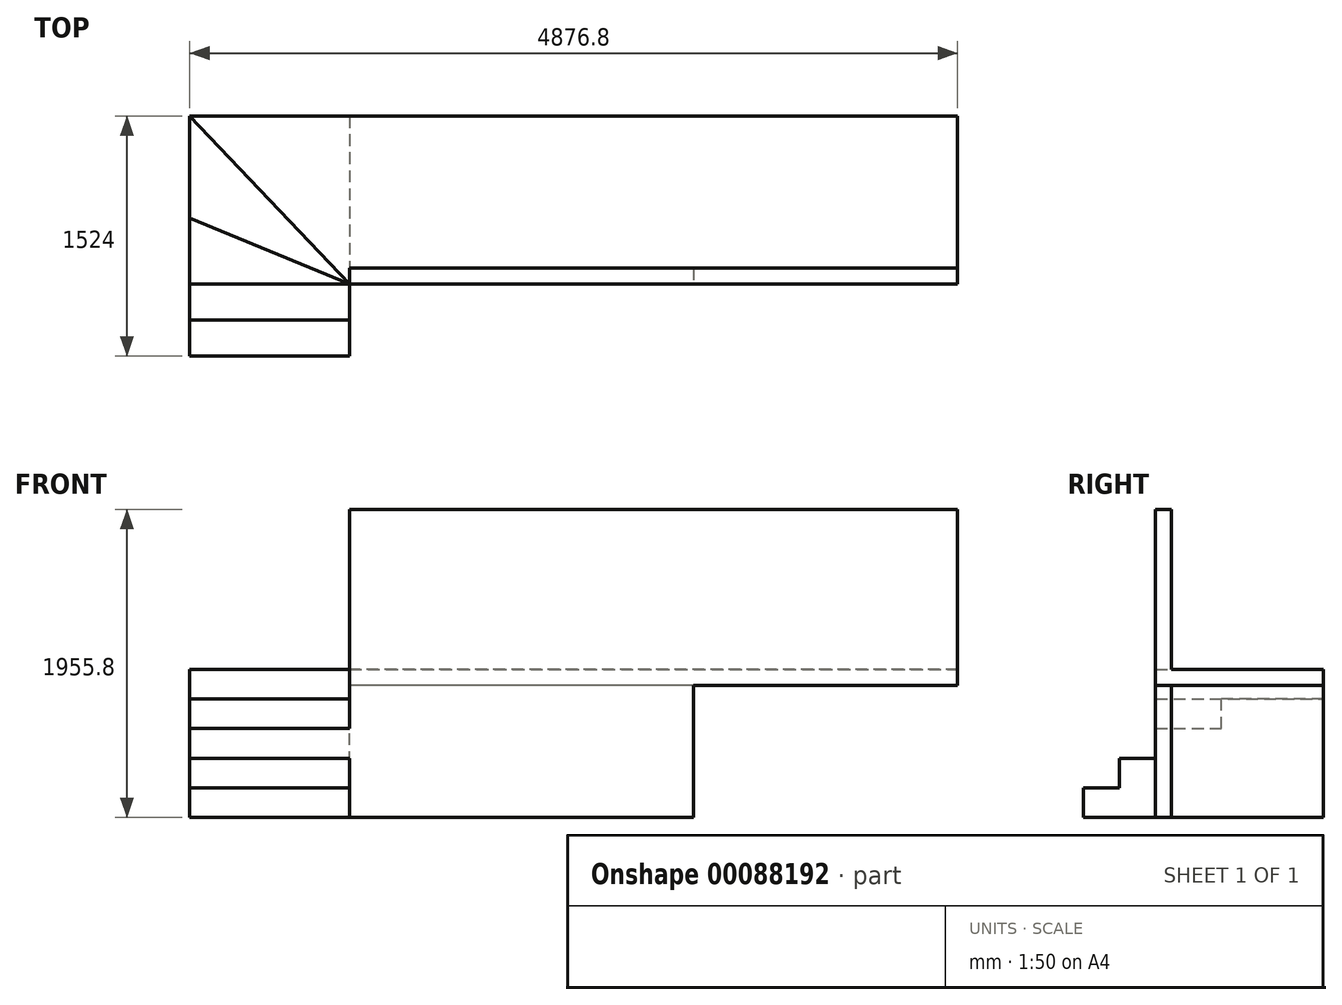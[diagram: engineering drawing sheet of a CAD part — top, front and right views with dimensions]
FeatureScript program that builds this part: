
annotation { "Feature Type Name" : "Feature", "Feature Type Description" : "" }
export const myFeature = defineFeature(function(context is Context, id is Id, definition is map)
    precondition{}
    {
        {
            var Q0;
            Q0=qCreatedBy(makeId("Top.planeOp"),FACE);
            var sketch = newSketch(context, id + "F0", { "sketchPlane" : qUnion([Q0])});
            skLineSegment(sketch, "E0.bottom", {"start": v(2438.4, -533.4) * mm, "end": v(-2438.4, -533.4) * mm});
            skLineSegment(sketch, "E0.top", {"start": v(2438.4, 533.4) * mm, "end": v(-2438.4, 533.4) * mm});
            skLineSegment(sketch, "E0.left", {"start": v(2438.4, -533.4) * mm, "end": v(2438.4, 533.4) * mm});
            skLineSegment(sketch, "E0.right", {"start": v(-2438.4, -533.4) * mm, "end": v(-2438.4, 533.4) * mm});
            skPoint(sketch, "E0.middle", {"position": v(0, 0) * mm});
            skSolve(sketch);
        }
        {
            var Q0;
            Q0=qSketchRegion(id+"F0",true);
            extrude(context, id + "F1", {"entities" : qUnion([Q0]), "oppositeDirection" : true, "depth" : 101.6 * mm});
        }
        {
            var Q0;
            Q0=makeQuery(id+"F1.opExtrude","SWEPT_FACE",FACE,{"disambiguationData":[OSD([sQuery(id+"F0.wireOp",EDGE,"E0.right")])]});
            var sketch = newSketch(context, id + "F2", { "sketchPlane" : qUnion([Q0])});
            skLineSegment(sketch, "E1", {"start": v(533.4, 0) * mm, "end": v(533.4, -187.96) * mm});
            skLineSegment(sketch, "E2", {"start": v(533.4, -187.96) * mm, "end": v(762, -187.96) * mm});
            skLineSegment(sketch, "E3", {"start": v(762, -187.96) * mm, "end": v(762, -375.92) * mm});
            skLineSegment(sketch, "E4", {"start": v(762, -375.92) * mm, "end": v(990.6, -375.92) * mm});
            skLineSegment(sketch, "E5", {"start": v(990.6, -375.92) * mm, "end": v(990.6, -563.88) * mm});
            skLineSegment(sketch, "E6", {"start": v(990.6, -563.88) * mm, "end": v(1219.2, -563.88) * mm});
            skLineSegment(sketch, "E7", {"start": v(1447.8, -751.84) * mm, "end": v(1447.8, -939.8) * mm});
            skLineSegment(sketch, "E8", {"start": v(1447.8, -939.8) * mm, "end": v(304.8, -939.8) * mm});
            skLineSegment(sketch, "E9", {"start": v(304.8, -939.8) * mm, "end": v(304.8, 0) * mm, "construction": true});
            skLineSegment(sketch, "E10", {"start": v(304.8, 0) * mm, "end": v(533.4, 0) * mm});
            skLineSegment(sketch, "E11", {"start": v(1219.2, -563.88) * mm, "end": v(1219.2, -751.84) * mm});
            skLineSegment(sketch, "E12", {"start": v(1219.2, -751.84) * mm, "end": v(1447.8, -751.84) * mm});
            skLineSegment(sketch, "E13", {"start": v(304.8, -939.8) * mm, "end": v(-533.4, -939.8) * mm});
            skLineSegment(sketch, "E14", {"start": v(-533.4, -939.8) * mm, "end": v(-533.4, 0) * mm});
            skLineSegment(sketch, "E15", {"start": v(-533.4, 0) * mm, "end": v(304.8, 0) * mm});
            skSolve(sketch);
        }
        {
            var Q0;
            Q0=qSketchRegion(id+"F2",true);
            extrude(context, id + "F3", {"entities" : qUnion([Q0]), "operationType" : NewBodyOperationType.ADD, "oppositeDirection" : true, "depth" : 1016 * mm});
        }
        {
            var Q0;
            Q0=makeQuery(id+"F3.boolean.opBoolean","MERGE",FACE,{"derivedFrom":[makeQuery(id+"F1.opExtrude","SWEPT_FACE",FACE,{"disambiguationData":[OSD([sQuery(id+"F0.wireOp",EDGE,"E0.bottom")])]}),makeQuery(id+"F3.opExtrude","SWEPT_FACE",FACE,{"disambiguationData":[OSD([sQuery(id+"F2.wireOp",EDGE,"E1")])]})]});
            var sketch = newSketch(context, id + "F4", { "sketchPlane" : qUnion([Q0])});
            skLineSegment(sketch, "E16.0", {"start": v(-1422.4, -101.6) * mm, "end": v(-1422.4, -187.96) * mm});
            skLineSegment(sketch, "E17", {"start": v(-1422.4, -101.6) * mm, "end": v(762, -101.6) * mm});
            skLineSegment(sketch, "E18", {"start": v(762, -101.6) * mm, "end": v(762, -939.8) * mm});
            skLineSegment(sketch, "E19", {"start": v(762, -939.8) * mm, "end": v(-1422.4, -939.8) * mm});
            skLineSegment(sketch, "E20", {"start": v(-1422.4, -187.96) * mm, "end": v(-1422.4, -939.8) * mm});
            skLineSegment(sketch, "E21.bottom", {"start": v(-812.8, -939.8) * mm, "end": v(-355.6, -939.8) * mm});
            skLineSegment(sketch, "E21.top", {"start": v(-812.8, -228.6) * mm, "end": v(-355.6, -228.6) * mm});
            skLineSegment(sketch, "E21.left", {"start": v(-812.8, -939.8) * mm, "end": v(-812.8, -228.6) * mm});
            skLineSegment(sketch, "E21.right", {"start": v(-355.6, -939.8) * mm, "end": v(-355.6, -228.6) * mm});
            skLineSegment(sketch, "E22.bottom", {"start": v(-304.8, -939.8) * mm, "end": v(152.4, -939.8) * mm});
            skLineSegment(sketch, "E22.top", {"start": v(-304.8, -228.6) * mm, "end": v(152.4, -228.6) * mm});
            skLineSegment(sketch, "E22.left", {"start": v(-304.8, -939.8) * mm, "end": v(-304.8, -228.6) * mm});
            skLineSegment(sketch, "E22.right", {"start": v(152.4, -939.8) * mm, "end": v(152.4, -228.6) * mm});
            skSolve(sketch);
        }
        {
            var Q0;
            Q0=makeQuery(id+"F4.imprint","IMPRINT",FACE,{"disambiguationData":[TD([[makeQuery(id+"F4.imprint","IMPRINT",EDGE,{"derivedFrom":sQuery(id+"F4.wireOp",EDGE,"E16.0")}),1.0]])]});
            extrude(context, id + "F5", {"entities" : qUnion([Q0]), "operationType" : NewBodyOperationType.ADD, "oppositeDirection" : true, "depth" : 101.6 * mm});
        }
        {
            var Q0;
            Q0=makeQuery(id+"F1.opExtrude","CAP_FACE",FACE,{"disambiguationData":[OSD([sQuery(id+"F0.wireOp",EDGE,"E0.bottom"),sQuery(id+"F0.wireOp",EDGE,"E0.top"),sQuery(id+"F0.wireOp",EDGE,"E0.left"),sQuery(id+"F0.wireOp",EDGE,"E0.right")])],"isStart":true});
            var sketch = newSketch(context, id + "F6", { "sketchPlane" : qUnion([Q0])});
            skLineSegment(sketch, "E23", {"start": v(-1422.4, -533.4) * mm, "end": v(-2438.4, 533.4) * mm});
            skLineSegment(sketch, "E24", {"start": v(-2438.4, 533.4) * mm, "end": v(-2438.4, -533.4) * mm});
            skLineSegment(sketch, "E25", {"start": v(-2438.4, -533.4) * mm, "end": v(-1422.4, -533.4) * mm});
            skSolve(sketch);
        }
        {
            var Q0;
            Q0 = qSketchRegion(id + "F6", true);
            extrude(context, id + "F7", {"entities" : qUnion([Q0]), "operationType" : NewBodyOperationType.REMOVE, "oppositeDirection" : true, "depth" : 187.96 * mm});
        }
        {
            var Q0;
            Q0=makeQuery(id+"F7.boolean.opBoolean","MERGE",FACE,{"derivedFrom":[makeQuery(id+"F3.opExtrude","SWEPT_FACE",FACE,{"disambiguationData":[OSD([sQuery(id+"F2.wireOp",EDGE,"E2")])]}),makeQuery(id+"F7.opExtrude","CAP_FACE",FACE,{"disambiguationData":[OSD([sQuery(id+"F6.wireOp",EDGE,"E23"),sQuery(id+"F6.wireOp",EDGE,"E24"),sQuery(id+"F6.wireOp",EDGE,"E25")])],"isStart":false})]});
            var sketch = newSketch(context, id + "F8", { "sketchPlane" : qUnion([Q0])});
            skLineSegment(sketch, "E26", {"start": v(-1422.4, -533.4) * mm, "end": v(-2438.4, -114.3) * mm});
            skLineSegment(sketch, "E27", {"start": v(-2438.4, -114.3) * mm, "end": v(-2438.4, -533.4) * mm});
            skLineSegment(sketch, "E28", {"start": v(-2438.4, -533.4) * mm, "end": v(-1422.4, -533.4) * mm, "construction": true});
            skLineSegment(sketch, "E29", {"start": v(-2438.4, 533.4) * mm, "end": v(-2438.4, -114.3) * mm, "construction": true});
            skLineSegment(sketch, "E30", {"start": v(-1422.4, -533.4) * mm, "end": v(-1422.4, -762) * mm});
            skLineSegment(sketch, "E31", {"start": v(-1422.4, -762) * mm, "end": v(-2438.4, -762) * mm});
            skLineSegment(sketch, "E32", {"start": v(-2438.4, -762) * mm, "end": v(-2438.4, -533.4) * mm});
            skSolve(sketch);
        }
        {
            var Q0;
            Q0 = qSketchRegion(id + "F8", true);
            extrude(context, id + "F9", {"entities" : qUnion([Q0]), "operationType" : NewBodyOperationType.REMOVE, "oppositeDirection" : true, "depth" : 187.96 * mm});
        }
        {
            var Q0;
            Q0=makeQuery(id+"F3.boolean.opBoolean","MERGE",FACE,{"derivedFrom":[makeQuery(id+"F1.opExtrude","SWEPT_FACE",FACE,{"disambiguationData":[OSD([sQuery(id+"F0.wireOp",EDGE,"E0.right")])]}),makeQuery(id+"F3.opExtrude","CAP_FACE",FACE,{"disambiguationData":[OSD([sQuery(id+"F2.wireOp",EDGE,"E1"),sQuery(id+"F2.wireOp",EDGE,"E2"),sQuery(id+"F2.wireOp",EDGE,"E3"),sQuery(id+"F2.wireOp",EDGE,"E4"),sQuery(id+"F2.wireOp",EDGE,"E5"),sQuery(id+"F2.wireOp",EDGE,"E6"),sQuery(id+"F2.wireOp",EDGE,"E7"),sQuery(id+"F2.wireOp",EDGE,"E8"),sQuery(id+"F2.wireOp",EDGE,"E10"),sQuery(id+"F2.wireOp",EDGE,"E11"),sQuery(id+"F2.wireOp",EDGE,"E12"),sQuery(id+"F2.wireOp",EDGE,"E13"),sQuery(id+"F2.wireOp",EDGE,"E14"),sQuery(id+"F2.wireOp",EDGE,"E15")])],"isStart":true})]});
            var sketch = newSketch(context, id + "F10", { "sketchPlane" : qUnion([Q0])});
            skLineSegment(sketch, "E33", {"start": v(533.4, -375.92) * mm, "end": v(533.4, -563.88) * mm});
            skLineSegment(sketch, "E34", {"start": v(533.4, -563.88) * mm, "end": v(762, -563.88) * mm});
            skLineSegment(sketch, "E35", {"start": v(762, -563.88) * mm, "end": v(762, -751.84) * mm});
            skLineSegment(sketch, "E36", {"start": v(762, -751.84) * mm, "end": v(990.6, -751.84) * mm});
            skLineSegment(sketch, "E37", {"start": v(990.6, -751.84) * mm, "end": v(990.6, -939.8) * mm});
            skLineSegment(sketch, "E38", {"start": v(990.6, -939.8) * mm, "end": v(1447.8, -939.8) * mm});
            skLineSegment(sketch, "E39", {"start": v(1447.8, -939.8) * mm, "end": v(1447.8, -375.92) * mm});
            skLineSegment(sketch, "E40", {"start": v(1447.8, -375.92) * mm, "end": v(533.4, -375.92) * mm});
            skSolve(sketch);
        }
        {
            var Q0;
            Q0 = qSketchRegion(id + "F10", true);
            extrude(context, id + "F11", {"entities" : qUnion([Q0]), "operationType" : NewBodyOperationType.REMOVE, "oppositeDirection" : true, "depth" : 1300.32 * mm});
        }
        {
            var Q0;
            Q0=makeQuery(id+"F3.boolean.opBoolean","MERGE",FACE,{"derivedFrom":[makeQuery(id+"F1.opExtrude","SWEPT_FACE",FACE,{"disambiguationData":[OSD([sQuery(id+"F0.wireOp",EDGE,"E0.bottom")])]}),makeQuery(id+"F3.opExtrude","SWEPT_FACE",FACE,{"disambiguationData":[OSD([sQuery(id+"F2.wireOp",EDGE,"E1")])]})]});
            var sketch = newSketch(context, id + "F12", { "sketchPlane" : qUnion([Q0])});
            skLineSegment(sketch, "E41", {"start": v(-1422.4, -101.6) * mm, "end": v(-1422.4, -939.8) * mm});
            skLineSegment(sketch, "E42", {"start": v(-1422.4, -939.8) * mm, "end": v(762, -939.8) * mm});
            skLineSegment(sketch, "E43", {"start": v(762, -939.8) * mm, "end": v(762, -101.6) * mm});
            skLineSegment(sketch, "E44", {"start": v(762, -101.6) * mm, "end": v(-1422.4, -101.6) * mm});
            skSolve(sketch);
        }
        {
            var Q0;
            Q0 = qSketchRegion(id + "F12", true);
            extrude(context, id + "F13", {"entities" : qUnion([Q0]), "operationType" : NewBodyOperationType.ADD, "oppositeDirection" : true, "depth" : 101.6 * mm});
        }
        {
            var Q0;
            Q0=makeQuery(id+"F1.opExtrude","CAP_FACE",FACE,{"disambiguationData":[OSD([sQuery(id+"F0.wireOp",EDGE,"E0.bottom"),sQuery(id+"F0.wireOp",EDGE,"E0.top"),sQuery(id+"F0.wireOp",EDGE,"E0.left"),sQuery(id+"F0.wireOp",EDGE,"E0.right")])],"isStart":true});
            var sketch = newSketch(context, id + "F14", { "sketchPlane" : qUnion([Q0])});
            skLineSegment(sketch, "E45.bottom", {"start": v(-1422.4, -533.4) * mm, "end": v(2438.4, -533.4) * mm});
            skLineSegment(sketch, "E45.top", {"start": v(-1422.4, -431.8) * mm, "end": v(2438.4, -431.8) * mm});
            skLineSegment(sketch, "E45.left", {"start": v(-1422.4, -533.4) * mm, "end": v(-1422.4, -431.8) * mm});
            skLineSegment(sketch, "E45.right", {"start": v(2438.4, -533.4) * mm, "end": v(2438.4, -431.8) * mm});
            skSolve(sketch);
        }
        {
            var Q0;
            Q0 = qSketchRegion(id + "F14", true);
            extrude(context, id + "F15", {"entities" : qUnion([Q0]), "operationType" : NewBodyOperationType.ADD, "depth" : 1016 * mm});
        }
    });
